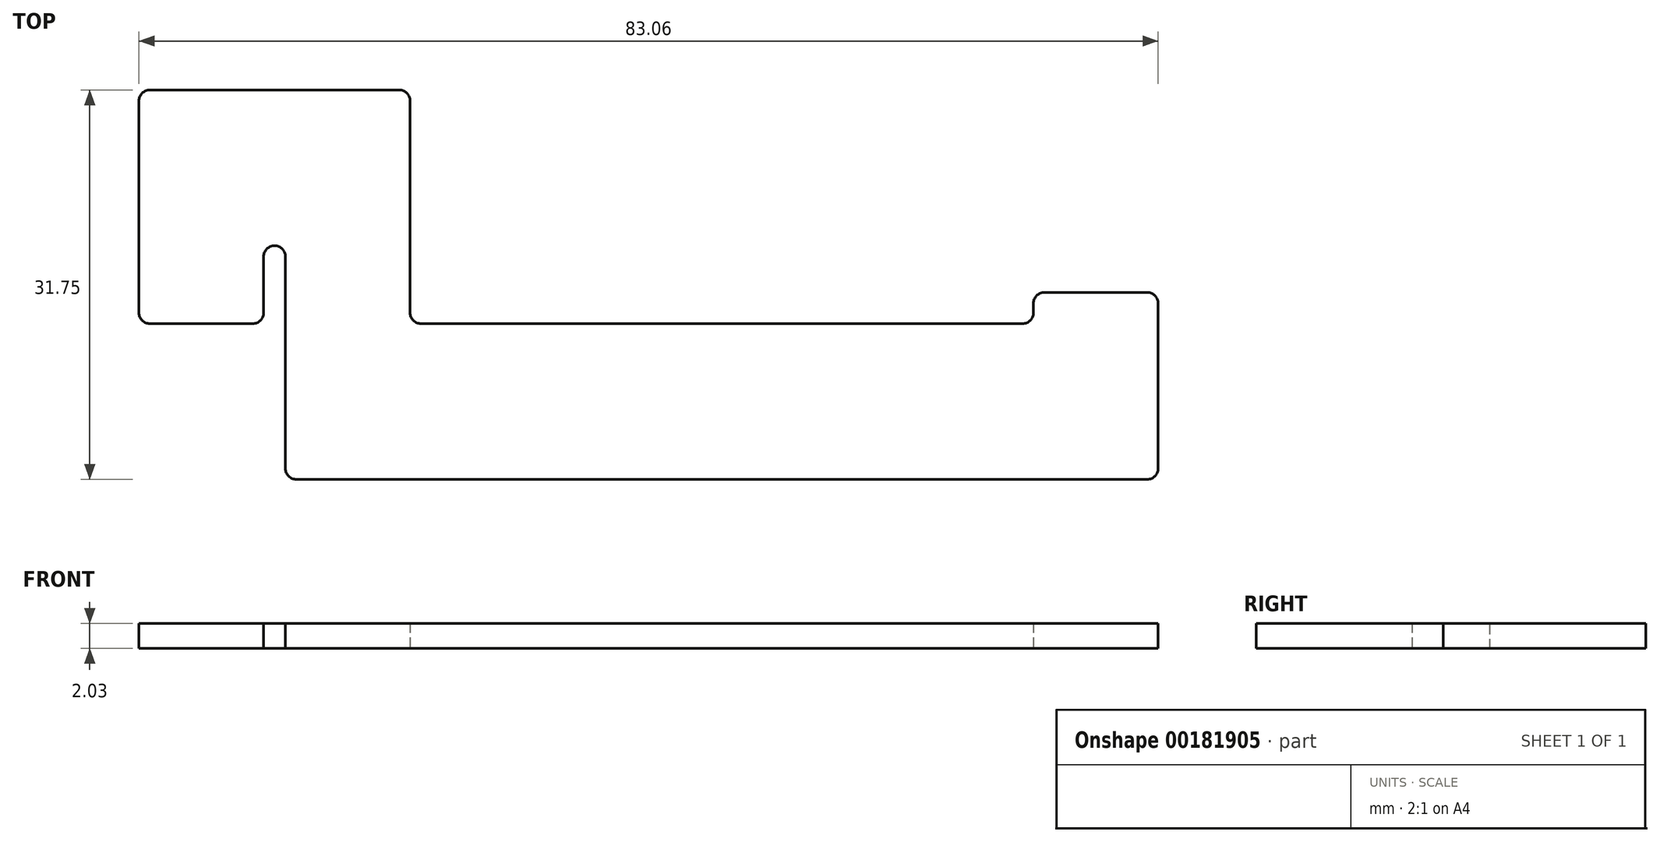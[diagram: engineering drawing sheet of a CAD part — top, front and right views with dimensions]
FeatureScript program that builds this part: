
annotation { "Feature Type Name" : "Feature", "Feature Type Description" : "" }
export const myFeature = defineFeature(function(context is Context, id is Id, definition is map)
    precondition{}
    {
        {
            var Q0;
            Q0=qCreatedBy(makeId("Top.planeOp"),FACE);
            var sketch = newSketch(context, id + "F0", { "sketchPlane" : qUnion([Q0])});
            skLineSegment(sketch, "E0", {"start": v(-11.05, -19.05) * mm, "end": v(-0.89, -19.05) * mm});
            skLineSegment(sketch, "E1", {"start": v(-0.89, -19.05) * mm, "end": v(-0.89, -12.7) * mm});
            skLineSegment(sketch, "E2", {"start": v(-0.89, -12.7) * mm, "end": v(0.89, -12.7) * mm});
            skLineSegment(sketch, "E3", {"start": v(0.89, -12.7) * mm, "end": v(0.89, -31.75) * mm});
            skLineSegment(sketch, "E4", {"start": v(0.89, -31.75) * mm, "end": v(72, -31.75) * mm});
            skLineSegment(sketch, "E5", {"start": v(72, -31.75) * mm, "end": v(72, -16.5) * mm});
            skLineSegment(sketch, "E6", {"start": v(72, -16.51) * mm, "end": v(61.85, -16.51) * mm});
            skLineSegment(sketch, "E7", {"start": v(61.85, -16.5) * mm, "end": v(61.85, -19.05) * mm});
            skLineSegment(sketch, "E8", {"start": v(61.85, -19.05) * mm, "end": v(11.05, -19.05) * mm});
            skLineSegment(sketch, "E9", {"start": v(11.05, -19.05) * mm, "end": v(11.05, 0) * mm});
            skLineSegment(sketch, "E10", {"start": v(11.05, 0) * mm, "end": v(-11.05, 0) * mm});
            skLineSegment(sketch, "E11", {"start": v(-11.05, 0) * mm, "end": v(-11.05, -19.05) * mm});
            skPoint(sketch, "E12", {"position": v(0, 0) * mm});
            skLineSegment(sketch, "E13", {"start": v(0.89, -12.7) * mm, "end": v(11.05, -12.7) * mm, "construction": true});
            skSolve(sketch);
        }
        {
            var Q0;
            Q0 = qSketchRegion(id + "F0", true);
            extrude(context, id + "F1", {"entities" : qUnion([Q0]), "depth" : 2.03 * mm});
        }
        {
            var Q0;
            Q0=makeQuery(id+"F1.opExtrude","SWEPT_EDGE",EDGE,{"disambiguationData":[OSD([sQuery(id+"F0.wireOp",EDGE,"E1"),sQuery(id+"F0.wireOp",EDGE,"E2")])]});
            var Q1;
            Q1=makeQuery(id+"F1.opExtrude","SWEPT_EDGE",EDGE,{"disambiguationData":[OSD([sQuery(id+"F0.wireOp",EDGE,"E2"),sQuery(id+"F0.wireOp",EDGE,"E3")])]});
            var Q2;
            Q2=makeQuery(id+"F1.opExtrude","SWEPT_EDGE",EDGE,{"disambiguationData":[OSD([sQuery(id+"F0.wireOp",EDGE,"E0"),sQuery(id+"F0.wireOp",EDGE,"E1")])]});
            var Q3;
            Q3=makeQuery(id+"F1.opExtrude","SWEPT_EDGE",EDGE,{"disambiguationData":[OSD([sQuery(id+"F0.wireOp",EDGE,"E0"),sQuery(id+"F0.wireOp",EDGE,"E11")])]});
            var Q4;
            Q4=makeQuery(id+"F1.opExtrude","SWEPT_EDGE",EDGE,{"disambiguationData":[OSD([sQuery(id+"F0.wireOp",EDGE,"E3"),sQuery(id+"F0.wireOp",EDGE,"E4")])]});
            var Q5;
            Q5=makeQuery(id+"F1.opExtrude","SWEPT_EDGE",EDGE,{"disambiguationData":[OSD([sQuery(id+"F0.wireOp",EDGE,"E8"),sQuery(id+"F0.wireOp",EDGE,"E9")])]});
            var Q6;
            Q6=makeQuery(id+"F1.opExtrude","SWEPT_EDGE",EDGE,{"disambiguationData":[OSD([sQuery(id+"F0.wireOp",EDGE,"E5"),sQuery(id+"F0.wireOp",EDGE,"E6")])]});
            var Q7;
            Q7=makeQuery(id+"F1.opExtrude","SWEPT_EDGE",EDGE,{"disambiguationData":[OSD([sQuery(id+"F0.wireOp",EDGE,"E4"),sQuery(id+"F0.wireOp",EDGE,"E5")])]});
            var Q8;
            Q8=makeQuery(id+"F1.opExtrude","SWEPT_EDGE",EDGE,{"disambiguationData":[OSD([sQuery(id+"F0.wireOp",EDGE,"E6"),sQuery(id+"F0.wireOp",EDGE,"E7")])]});
            var Q9;
            Q9=makeQuery(id+"F1.opExtrude","SWEPT_EDGE",EDGE,{"disambiguationData":[OSD([sQuery(id+"F0.wireOp",EDGE,"E7"),sQuery(id+"F0.wireOp",EDGE,"E8")])]});
            var Q10;
            Q10=makeQuery(id+"F1.opExtrude","SWEPT_EDGE",EDGE,{"disambiguationData":[OSD([sQuery(id+"F0.wireOp",EDGE,"E9"),sQuery(id+"F0.wireOp",EDGE,"E10")])]});
            var Q11;
            Q11=makeQuery(id+"F1.opExtrude","SWEPT_EDGE",EDGE,{"disambiguationData":[OSD([sQuery(id+"F0.wireOp",EDGE,"E10"),sQuery(id+"F0.wireOp",EDGE,"E11")])]});
            fillet(context, id + "F2", {"entities" : qUnion([Q0, Q1, Q2, Q3, Q4, Q5, Q6, Q7, Q8, Q9, Q10, Q11]), "radius" : 0.89 * mm, "tangentPropagation" : true, "allowEdgeOverflow" : false});
        }
    });
